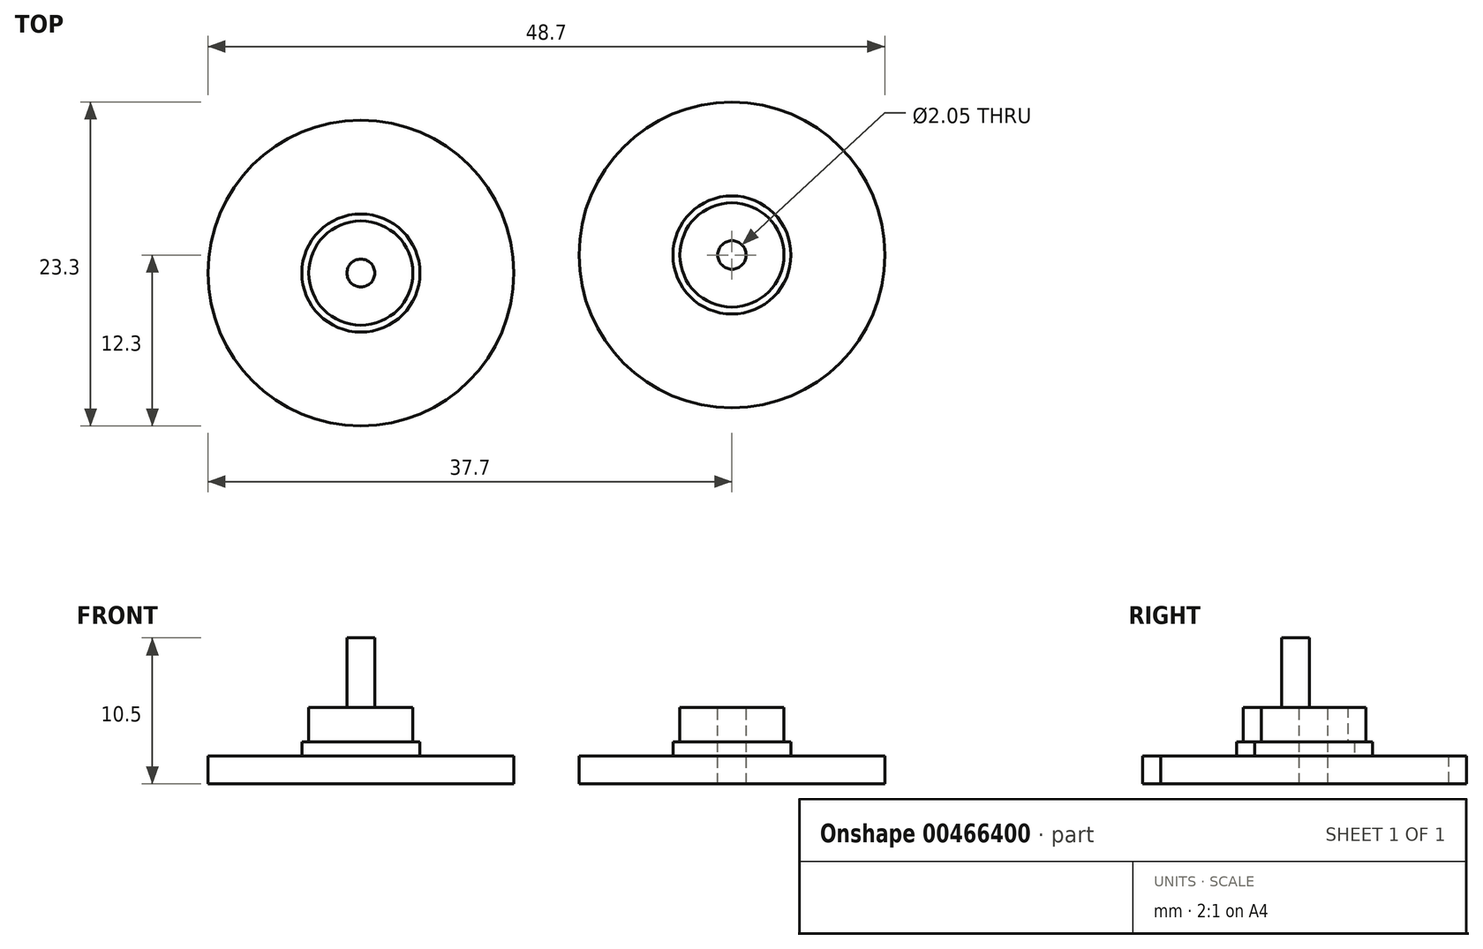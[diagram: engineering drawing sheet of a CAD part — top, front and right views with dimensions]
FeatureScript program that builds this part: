
annotation { "Feature Type Name" : "Feature", "Feature Type Description" : "" }
export const myFeature = defineFeature(function(context is Context, id is Id, definition is map)
    precondition{}
    {
        {
            var Q0;
            Q0=qCreatedBy(makeId("Top.planeOp"),FACE);
            var sketch = newSketch(context, id + "F0", { "sketchPlane" : qUnion([Q0])});
            skCircle(sketch, "E0", {"center": v(0, 0) * mm, "radius": 3.75 * mm});
            skCircle(sketch, "E1", {"center": v(0, 0) * mm, "radius": 4.25 * mm});
            skCircle(sketch, "E2", {"center": v(0, 0) * mm, "radius": 11 * mm});
            skSolve(sketch);
        }
        {
            var Q0;
            Q0=makeQuery(id+"F0.imprint","IMPRINT",FACE,{"disambiguationData":[TD([[makeQuery(id+"F0.imprint","IMPRINT",EDGE,{"derivedFrom":sQuery(id+"F0.wireOp",EDGE,"E0")}),1.0]])]});
            extrude(context, id + "F1", {"entities" : qUnion([Q0]), "depth" : 5.5 * mm});
        }
        {
            var Q0;
            Q0=makeQuery(id+"F0.imprint","IMPRINT",FACE,{"disambiguationData":[TD([[makeQuery(id+"F0.imprint","IMPRINT",EDGE,{"derivedFrom":sQuery(id+"F0.wireOp",EDGE,"E0")}),-1.0]])]});
            extrude(context, id + "F2", {"entities" : qUnion([Q0]), "operationType" : NewBodyOperationType.ADD, "depth" : 3 * mm});
        }
        {
            var Q0;
            Q0=makeQuery(id+"F0.imprint","IMPRINT",FACE,{"disambiguationData":[TD([[makeQuery(id+"F0.imprint","IMPRINT",EDGE,{"derivedFrom":sQuery(id+"F0.wireOp",EDGE,"E1")}),-1.0]])]});
            extrude(context, id + "F3", {"entities" : qUnion([Q0]), "operationType" : NewBodyOperationType.ADD, "depth" : 2 * mm});
        }
        {
            var Q0;
            Q0=makeQuery(id+"F1.opExtrude","SWEPT_BODY",BODY,{"disambiguationData":[OSD([sQuery(id+"F0.wireOp",EDGE,"E0")])]});
            transform(context, id + "F4", {"entities" : qUnion([Q0]), "transformType" : TransformType.TRANSLATION_3D, "dx" : 26.7 * mm, "dy" : 1.3 * mm, "dz" : 0 * mm, "makeCopy" : true});
        }
        {
            var Q0;
            Q0=makeQuery(id+"F1.opExtrude","CAP_FACE",FACE,{"disambiguationData":[OSD([sQuery(id+"F0.wireOp",EDGE,"E0")])],"isStart":false});
            var sketch = newSketch(context, id + "F5", { "sketchPlane" : qUnion([Q0])});
            skCircle(sketch, "E3", {"center": v(0, 0) * mm, "radius": 1 * mm});
            skSolve(sketch);
        }
        {
            var Q0;
            Q0=makeQuery(id+"F5.imprint","IMPRINT",FACE,{"disambiguationData":[TD([[makeQuery(id+"F5.imprint","IMPRINT",EDGE,{"derivedFrom":sQuery(id+"F5.wireOp",EDGE,"E3")}),1.0]])]});
            extrude(context, id + "F6", {"entities" : qUnion([Q0]), "operationType" : NewBodyOperationType.ADD, "depth" : 5 * mm});
        }
        {
            var Q0;
            Q0=makeQuery(id+"F4.opPattern","COPY",FACE,{"derivedFrom":makeQuery(id+"F1.opExtrude","CAP_FACE",FACE,{"disambiguationData":[OSD([sQuery(id+"F0.wireOp",EDGE,"E0")])],"isStart":false}),"instanceName":"1"});
            var sketch = newSketch(context, id + "F7", { "sketchPlane" : qUnion([Q0])});
            skCircle(sketch, "E4", {"center": v(26.7, 1.3) * mm, "radius": 1.02 * mm});
            skSolve(sketch);
        }
        {
            var Q0;
            Q0=makeQuery(id+"F7.imprint","IMPRINT",FACE,{"disambiguationData":[TD([[makeQuery(id+"F7.imprint","IMPRINT",EDGE,{"derivedFrom":sQuery(id+"F7.wireOp",EDGE,"E4")}),1.0]])]});
            extrude(context, id + "F8", {"entities" : qUnion([Q0]), "operationType" : NewBodyOperationType.REMOVE, "oppositeDirection" : true, "depth" : 7.7 * mm});
        }
    });
